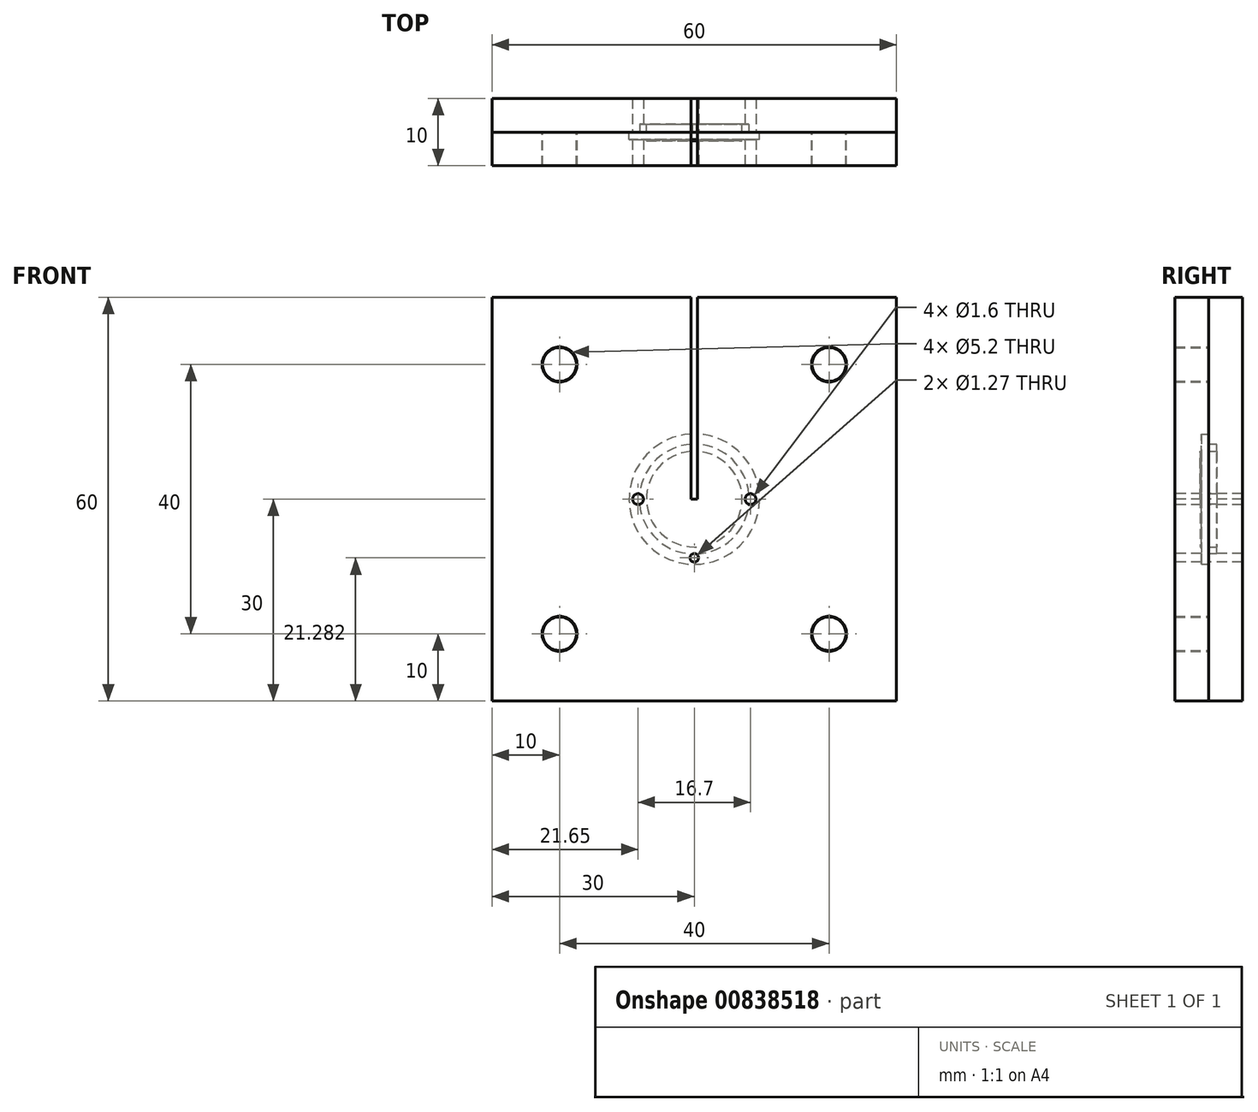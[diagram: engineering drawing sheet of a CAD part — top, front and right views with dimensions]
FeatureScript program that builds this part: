
annotation { "Feature Type Name" : "Feature", "Feature Type Description" : "" }
export const myFeature = defineFeature(function(context is Context, id is Id, definition is map)
    precondition{}
    {
        {
            var Q0;
            Q0=qCreatedBy(makeId("Front.planeOp"),FACE);
            var sketch = newSketch(context, id + "F0", { "sketchPlane" : qUnion([Q0])});
            skLineSegment(sketch, "E0.bottom", {"start": v(30, 30) * mm, "end": v(-30, 30) * mm});
            skLineSegment(sketch, "E0.top", {"start": v(30, -30) * mm, "end": v(-30, -30) * mm});
            skLineSegment(sketch, "E0.left", {"start": v(30, 30) * mm, "end": v(30, -30) * mm});
            skLineSegment(sketch, "E0.right", {"start": v(-30, 30) * mm, "end": v(-30, -30) * mm});
            skPoint(sketch, "E0.middle", {"position": v(0, 0) * mm});
            skSolve(sketch);
        }
        {
            var Q0;
            Q0 = qSketchRegion(id + "F0", true);
            extrude(context, id + "F1", {"entities" : qUnion([Q0]), "endBound" : BoundingType.SYMMETRIC, "depth" : 5 * mm, "offsetDistance" : 25 * mm});
        }
        {
            var Q0;
            Q0=makeQuery(id+"F1.opExtrude","CAP_FACE",FACE,{"disambiguationData":[OSD([sQuery(id+"F0.wireOp",EDGE,"E0.bottom"),sQuery(id+"F0.wireOp",EDGE,"E0.top"),sQuery(id+"F0.wireOp",EDGE,"E0.left"),sQuery(id+"F0.wireOp",EDGE,"E0.right")])],"isStart":false});
            var sketch = newSketch(context, id + "F2", { "sketchPlane" : qUnion([Q0])});
            skCircle(sketch, "E1", {"center": v(0, 0) * mm, "radius": 8.15 * mm});
            skSolve(sketch);
        }
        {
            var Q0;
            Q0 = qSketchRegion(id + "F2", true);
            extrude(context, id + "F3", {"entities" : qUnion([Q0]), "operationType" : NewBodyOperationType.REMOVE, "oppositeDirection" : true, "depth" : 1.2 * mm, "offsetDistance" : 25 * mm});
        }
        {
            var Q0;
            Q0=makeQuery(id+"F3.boolean.opBoolean","COPY",FACE,{"derivedFrom":makeQuery(id+"F3.opExtrude","CAP_FACE",FACE,{"disambiguationData":[OSD([sQuery(id+"F2.wireOp",EDGE,"E1")])],"isStart":false})});
            var sketch = newSketch(context, id + "F4", { "sketchPlane" : qUnion([Q0])});
            skCircle(sketch, "E2", {"center": v(0, 0) * mm, "radius": 7.1 * mm});
            skSolve(sketch);
        }
        {
            var Q0;
            Q0 = qSketchRegion(id + "F4", true);
            extrude(context, id + "F5", {"entities" : qUnion([Q0]), "operationType" : NewBodyOperationType.ADD, "depth" : 2.5 * mm, "offsetDistance" : 25 * mm});
        }
        {
            var Q0;
            Q0=makeQuery(id+"F1.opExtrude","CAP_FACE",FACE,{"disambiguationData":[OSD([sQuery(id+"F0.wireOp",EDGE,"E0.bottom"),sQuery(id+"F0.wireOp",EDGE,"E0.top"),sQuery(id+"F0.wireOp",EDGE,"E0.left"),sQuery(id+"F0.wireOp",EDGE,"E0.right")])],"isStart":false});
            var sketch = newSketch(context, id + "F6", { "sketchPlane" : qUnion([Q0])});
            skLineSegment(sketch, "E3", {"start": v(0, 0) * mm, "end": v(20, 0) * mm, "construction": true});
            skLineSegment(sketch, "E4", {"start": v(20, 0) * mm, "end": v(20, 20) * mm, "construction": true});
            skLineSegment(sketch, "E5", {"start": v(20, 20) * mm, "end": v(-20, 20) * mm, "construction": true});
            skLineSegment(sketch, "E6", {"start": v(-20, 20) * mm, "end": v(-20, -20) * mm, "construction": true});
            skLineSegment(sketch, "E7", {"start": v(-20, -20) * mm, "end": v(20, -20) * mm, "construction": true});
            skCircle(sketch, "E8", {"center": v(-20, 20) * mm, "radius": 2.5 * mm});
            skCircle(sketch, "E9", {"center": v(20, 20) * mm, "radius": 2.5 * mm});
            skCircle(sketch, "E10", {"center": v(20, -20) * mm, "radius": 2.5 * mm});
            skCircle(sketch, "E11", {"center": v(-20, -20) * mm, "radius": 2.5 * mm});
            skSolve(sketch);
        }
        {
            var Q0;
            Q0 = qSketchRegion(id + "F6", true);
            extrude(context, id + "F7", {"entities" : qUnion([Q0]), "operationType" : NewBodyOperationType.ADD, "depth" : 5 * mm, "offsetDistance" : 25 * mm});
        }
        {
            var Q0;
            Q0=makeQuery(id+"F1.opExtrude","CAP_FACE",FACE,{"disambiguationData":[OSD([sQuery(id+"F0.wireOp",EDGE,"E0.bottom"),sQuery(id+"F0.wireOp",EDGE,"E0.top"),sQuery(id+"F0.wireOp",EDGE,"E0.left"),sQuery(id+"F0.wireOp",EDGE,"E0.right")])],"isStart":false});
            var sketch = newSketch(context, id + "F8", { "sketchPlane" : qUnion([Q0])});
            skLineSegment(sketch, "E12.0", {"start": v(30, -30) * mm, "end": v(-30, -30) * mm});
            skLineSegment(sketch, "E13.0", {"start": v(30, 30) * mm, "end": v(30, -30) * mm});
            skLineSegment(sketch, "E14.0", {"start": v(30, 30) * mm, "end": v(-30, 30) * mm});
            skLineSegment(sketch, "E15.0", {"start": v(-30, 30) * mm, "end": v(-30, -30) * mm});
            skCircle(sketch, "E16", {"center": v(20, 20) * mm, "radius": 2.6 * mm});
            skCircle(sketch, "E17", {"center": v(-20, -20) * mm, "radius": 2.6 * mm});
            skCircle(sketch, "E18", {"center": v(20, -20) * mm, "radius": 2.6 * mm});
            skCircle(sketch, "E19", {"center": v(-20, 20) * mm, "radius": 2.6 * mm});
            skSolve(sketch);
        }
        {
            var Q0;
            Q0 = qSketchRegion(id + "F8", true);
            extrude(context, id + "F9", {"entities" : qUnion([Q0]), "depth" : 5 * mm, "offsetDistance" : 25 * mm});
        }
        {
            var Q0;
            Q0=makeQuery(id+"F9.opExtrude","CAP_FACE",FACE,{"disambiguationData":[OSD([sQuery(id+"F8.wireOp",EDGE,"E12.0"),sQuery(id+"F8.wireOp",EDGE,"E13.0"),sQuery(id+"F8.wireOp",EDGE,"E14.0"),sQuery(id+"F8.wireOp",EDGE,"E15.0"),sQuery(id+"F8.wireOp",EDGE,"E16"),sQuery(id+"F8.wireOp",EDGE,"E17"),sQuery(id+"F8.wireOp",EDGE,"E18"),sQuery(id+"F8.wireOp",EDGE,"E19")])],"isStart":true});
            var sketch = newSketch(context, id + "F10", { "sketchPlane" : qUnion([Q0])});
            skCircle(sketch, "E20", {"center": v(0, 0) * mm, "radius": 9.68 * mm});
            skSolve(sketch);
        }
        {
            var Q0;
            Q0 = qSketchRegion(id + "F10", true);
            extrude(context, id + "F11", {"entities" : qUnion([Q0]), "operationType" : NewBodyOperationType.REMOVE, "oppositeDirection" : true, "depth" : 1.1 * mm, "offsetDistance" : 25 * mm});
        }
        {
            var Q0;
            Q0=makeQuery(id+"F9.opExtrude","CAP_FACE",FACE,{"disambiguationData":[OSD([sQuery(id+"F8.wireOp",EDGE,"E12.0"),sQuery(id+"F8.wireOp",EDGE,"E13.0"),sQuery(id+"F8.wireOp",EDGE,"E14.0"),sQuery(id+"F8.wireOp",EDGE,"E15.0"),sQuery(id+"F8.wireOp",EDGE,"E16"),sQuery(id+"F8.wireOp",EDGE,"E17"),sQuery(id+"F8.wireOp",EDGE,"E18"),sQuery(id+"F8.wireOp",EDGE,"E19")])],"isStart":false});
            var sketch = newSketch(context, id + "F12", { "sketchPlane" : qUnion([Q0])});
            skLineSegment(sketch, "E21", {"start": v(0.45, 0) * mm, "end": v(0.45, 33) * mm});
            skLineSegment(sketch, "E22", {"start": v(-0.45, 0) * mm, "end": v(-0.45, 33) * mm});
            skLineSegment(sketch, "E23", {"start": v(-0.45, 33) * mm, "end": v(0.45, 33) * mm});
            skLineSegment(sketch, "E24", {"start": v(-0.45, 0) * mm, "end": v(0.45, 0) * mm});
            skSolve(sketch);
        }
        {
            var Q0;
            Q0 = qSketchRegion(id + "F12", true);
            extrude(context, id + "F13", {"entities" : qUnion([Q0]), "operationType" : NewBodyOperationType.REMOVE, "oppositeDirection" : true, "depth" : 25 * mm, "offsetDistance" : 25 * mm});
        }
        {
            var Q0;
            Q0=makeQuery(id+"F9.opExtrude","CAP_FACE",FACE,{"disambiguationData":[OSD([sQuery(id+"F8.wireOp",EDGE,"E12.0"),sQuery(id+"F8.wireOp",EDGE,"E13.0"),sQuery(id+"F8.wireOp",EDGE,"E14.0"),sQuery(id+"F8.wireOp",EDGE,"E15.0"),sQuery(id+"F8.wireOp",EDGE,"E16"),sQuery(id+"F8.wireOp",EDGE,"E17"),sQuery(id+"F8.wireOp",EDGE,"E18"),sQuery(id+"F8.wireOp",EDGE,"E19")])],"isStart":false});
            var sketch = newSketch(context, id + "F14", { "sketchPlane" : qUnion([Q0])});
            skLineSegment(sketch, "E25", {"start": v(0, 0) * mm, "end": v(-8.35, 0) * mm, "construction": true});
            skCircle(sketch, "E26", {"center": v(-8.35, 0) * mm, "radius": 0.8 * mm});
            skLineSegment(sketch, "E27", {"start": v(0, 0) * mm, "end": v(0, 3.8) * mm, "construction": true});
            skCircle(sketch, "E28.MirrorC", {"center": v(8.35, 0) * mm, "radius": 0.8 * mm});
            skSolve(sketch);
        }
        {
            var Q0;
            Q0 = qSketchRegion(id + "F14", true);
            extrude(context, id + "F15", {"entities" : qUnion([Q0]), "operationType" : NewBodyOperationType.REMOVE, "oppositeDirection" : true, "depth" : 25 * mm, "offsetDistance" : 25 * mm});
        }
        {
            var Q0;
            Q0=makeQuery(id+"F9.opExtrude","CAP_FACE",FACE,{"disambiguationData":[OSD([sQuery(id+"F8.wireOp",EDGE,"E12.0"),sQuery(id+"F8.wireOp",EDGE,"E13.0"),sQuery(id+"F8.wireOp",EDGE,"E14.0"),sQuery(id+"F8.wireOp",EDGE,"E15.0"),sQuery(id+"F8.wireOp",EDGE,"E16"),sQuery(id+"F8.wireOp",EDGE,"E17"),sQuery(id+"F8.wireOp",EDGE,"E18"),sQuery(id+"F8.wireOp",EDGE,"E19")])],"isStart":false});
            var sketch = newSketch(context, id + "F16", { "sketchPlane" : qUnion([Q0])});
            skCircle(sketch, "E29", {"center": v(0, -8.72) * mm, "radius": 0.64 * mm});
            skSolve(sketch);
        }
        {
            var Q0;
            Q0 = qSketchRegion(id + "F16", true);
            extrude(context, id + "F17", {"entities" : qUnion([Q0]), "operationType" : NewBodyOperationType.REMOVE, "oppositeDirection" : true, "depth" : 25 * mm, "offsetDistance" : 25 * mm});
        }
    });
